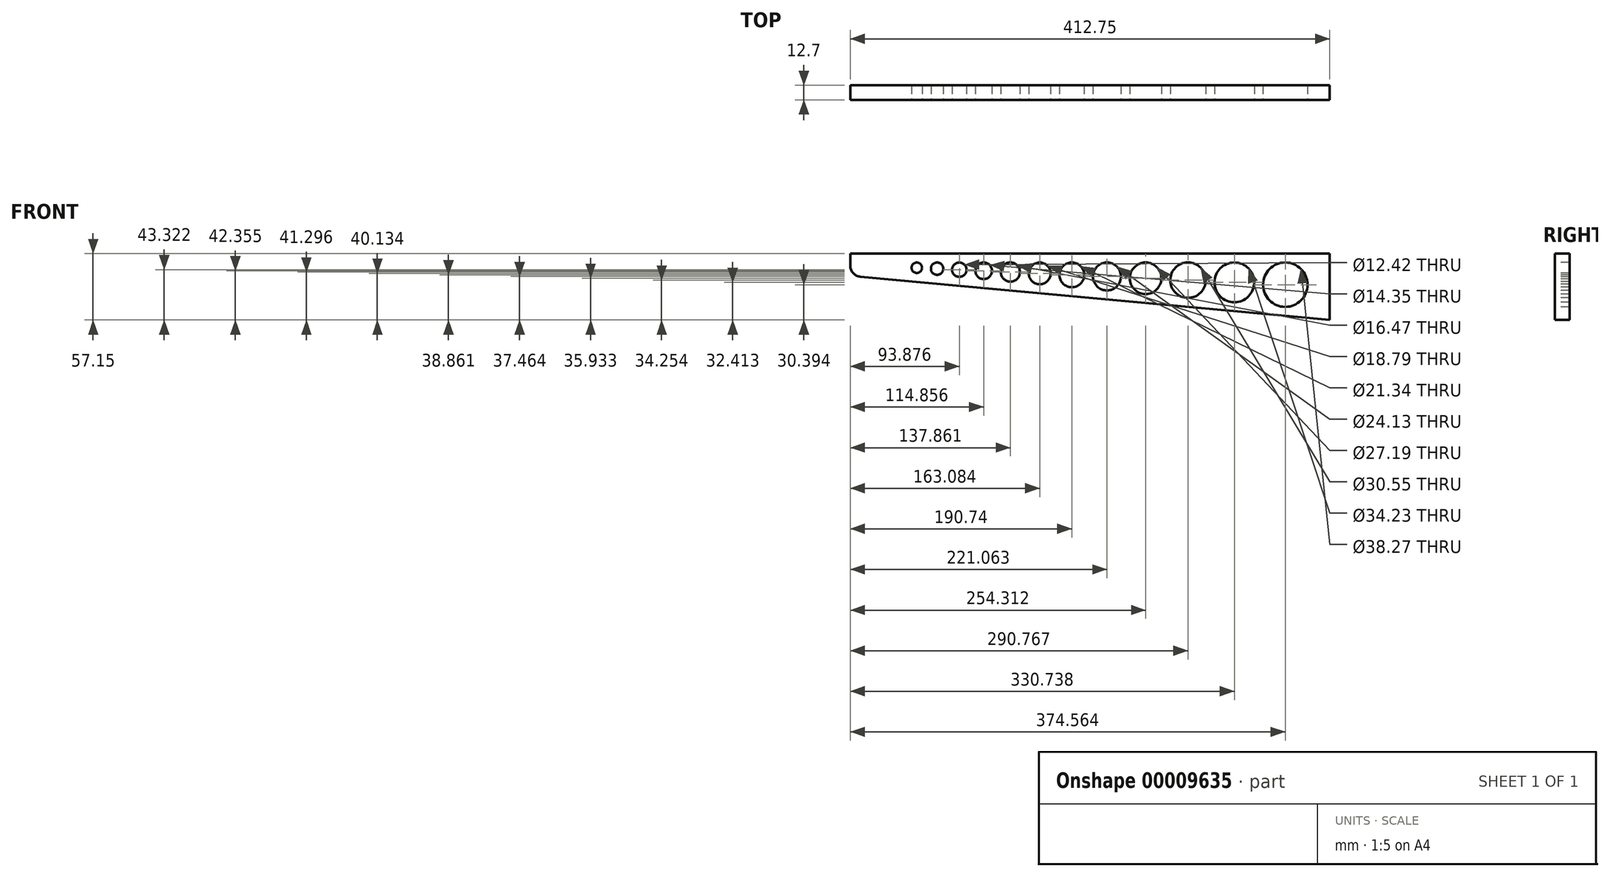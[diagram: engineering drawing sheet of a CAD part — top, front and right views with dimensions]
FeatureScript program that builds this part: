
annotation { "Feature Type Name" : "Feature", "Feature Type Description" : "" }
export const myFeature = defineFeature(function(context is Context, id is Id, definition is map)
    precondition{}
    {
        {
            var Q0;
            Q0=qCreatedBy(makeId("Front.planeOp"),FACE);
            var sketch = newSketch(context, id + "F0", { "sketchPlane" : qUnion([Q0])});
            skLineSegment(sketch, "E0", {"start": v(0, 0) * mm, "end": v(-412.75, 0) * mm});
            skLineSegment(sketch, "E1", {"start": v(-412.75, 0) * mm, "end": v(-412.75, -10.36) * mm});
            skLineSegment(sketch, "E2", {"start": v(-404.1, -19.85) * mm, "end": v(0, -57.15) * mm});
            skLineSegment(sketch, "E3", {"start": v(0, -57.15) * mm, "end": v(0, 0) * mm});
            skPoint(sketch, "E4.visualSharp", {"position": v(-412.75, -19.05) * mm});
            skArc(sketch, "E4.filletArc", {"start": v(-412.75, -10.36) * mm, "mid": v(-410.26, -16.78) * mm, "end": v(-404.1, -19.85) * mm});
            skSolve(sketch);
        }
        {
            var Q0;
            Q0=makeQuery(id+"F0.imprint","IMPRINT",FACE,{"disambiguationData":[TD([[makeQuery(id+"F0.imprint","IMPRINT",EDGE,{"derivedFrom":sQuery(id+"F0.wireOp",EDGE,"E0")}),1.0]])]});
            extrude(context, id + "F1", {"entities" : qUnion([Q0]), "depth" : 12.7 * mm});
        }
        {
            var Q0;
            Q0=makeQuery(id+"F1.opExtrude","CAP_FACE",FACE,{"disambiguationData":[OSD([sQuery(id+"F0.wireOp",EDGE,"E0"),sQuery(id+"F0.wireOp",EDGE,"E1"),sQuery(id+"F0.wireOp",EDGE,"E2"),sQuery(id+"F0.wireOp",EDGE,"E3"),sQuery(id+"F0.wireOp",EDGE,"E4.filletArc")])],"isStart":false});
            var sketch = newSketch(context, id + "F2", { "sketchPlane" : qUnion([Q0])});
            skLineSegment(sketch, "E5", {"start": v(0, 0) * mm, "end": v(0, -7.62) * mm, "construction": true});
            skLineSegment(sketch, "E6", {"start": v(0, -7.62) * mm, "end": v(-453.67, -7.62) * mm, "construction": true});
            skLineSegment(sketch, "E7", {"start": v(0, -57.15) * mm, "end": v(0.7, -49.56) * mm, "construction": true});
            skLineSegment(sketch, "E8", {"start": v(0.7, -49.56) * mm, "end": v(-453.67, -7.62) * mm, "construction": true});
            skCircle(sketch, "E9", {"center": v(-38.19, -26.76) * mm, "radius": 19.14 * mm});
            skCircle(sketch, "E10", {"center": v(-82.01, -24.74) * mm, "radius": 17.12 * mm});
            skCircle(sketch, "E11", {"center": v(-121.98, -22.9) * mm, "radius": 15.28 * mm});
            skCircle(sketch, "E12", {"center": v(-158.44, -21.22) * mm, "radius": 13.6 * mm});
            skCircle(sketch, "E13", {"center": v(-191.69, -19.69) * mm, "radius": 12.07 * mm});
            skCircle(sketch, "E14", {"center": v(-222.01, -18.29) * mm, "radius": 10.67 * mm});
            skCircle(sketch, "E15", {"center": v(-249.67, -17.02) * mm, "radius": 9.4 * mm});
            skCircle(sketch, "E16", {"center": v(-274.89, -15.85) * mm, "radius": 8.23 * mm});
            skCircle(sketch, "E17", {"center": v(-297.9, -14.8) * mm, "radius": 7.17 * mm});
            skCircle(sketch, "E18", {"center": v(-318.87, -13.83) * mm, "radius": 6.2 * mm});
            skCircle(sketch, "E19", {"center": v(-338, -12.95) * mm, "radius": 5.33 * mm});
            skCircle(sketch, "E20", {"center": v(-355.46, -12.14) * mm, "radius": 4.52 * mm});
            skSolve(sketch);
        }
        {
            var Q0;
            Q0=qSketchRegion(id+"F2",true);
            extrude(context, id + "F3", {"entities" : qUnion([Q0]), "operationType" : NewBodyOperationType.REMOVE, "endBound" : BoundingType.THROUGH_ALL, "oppositeDirection" : true, "depth" : 25.4 * mm});
        }
    });
